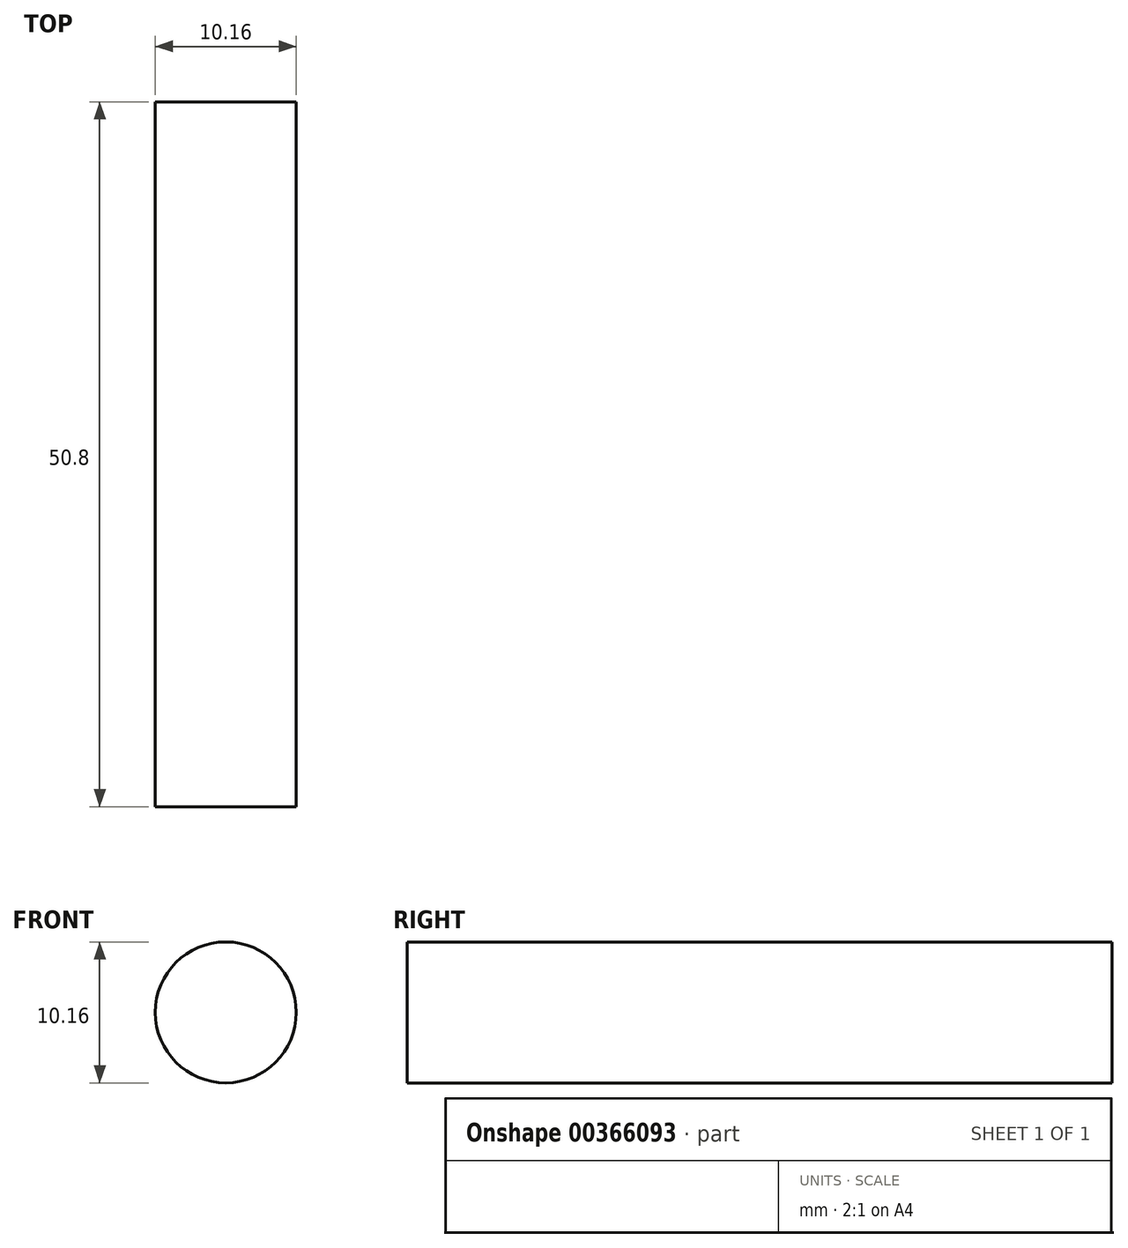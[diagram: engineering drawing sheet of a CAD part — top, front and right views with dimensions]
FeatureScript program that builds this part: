
annotation { "Feature Type Name" : "Feature", "Feature Type Description" : "" }
export const myFeature = defineFeature(function(context is Context, id is Id, definition is map)
    precondition{}
    {
        {
            var Q0;
            Q0=qCreatedBy(makeId("Front.planeOp"),FACE);
            var sketch = newSketch(context, id + "F0", { "sketchPlane" : qUnion([Q0])});
            skCircle(sketch, "E0", {"center": v(0, 0) * mm, "radius": 5.08 * mm});
            skSolve(sketch);
        }
        {
            var Q0;
            Q0=makeQuery(id+"F0.imprint","IMPRINT",FACE,{"disambiguationData":[TD([[makeQuery(id+"F0.imprint","IMPRINT",EDGE,{"derivedFrom":sQuery(id+"F0.wireOp",EDGE,"E0")}),1.0]])]});
            extrude(context, id + "F1", {"entities" : qUnion([Q0]), "depth" : 50.8 * mm});
        }
    });
